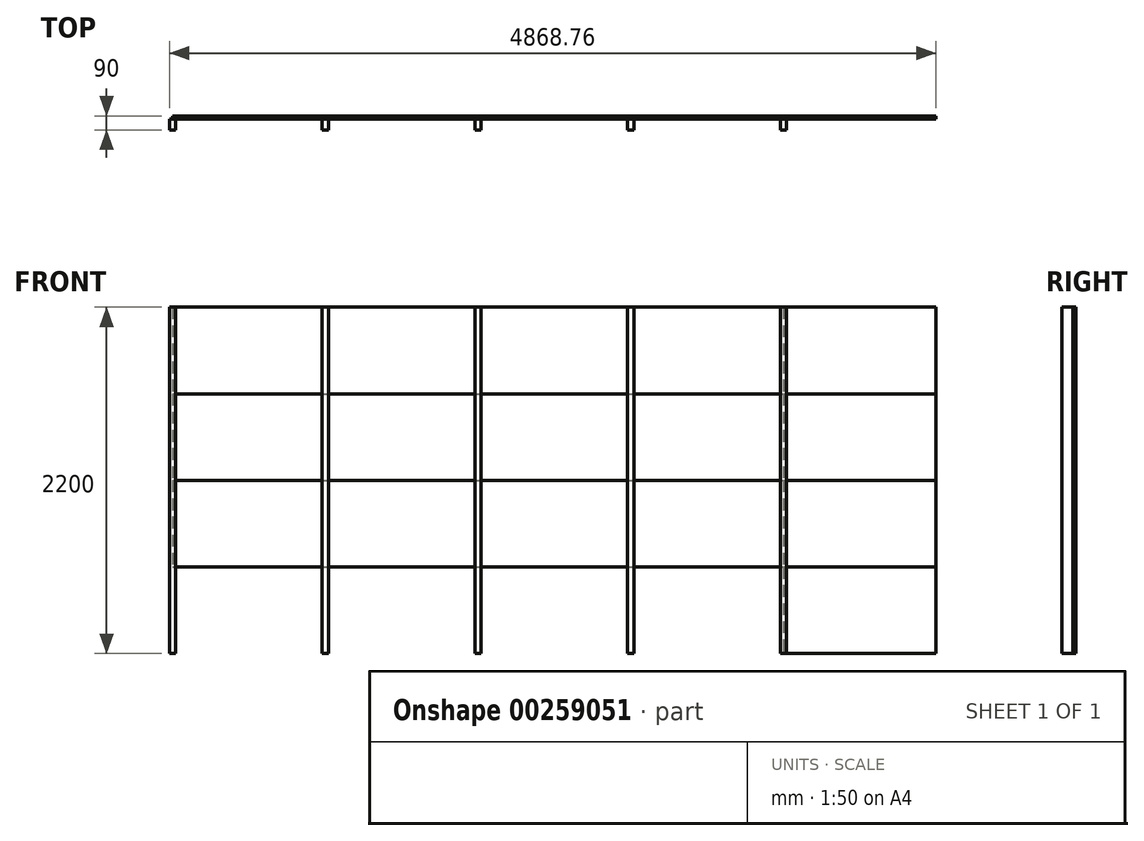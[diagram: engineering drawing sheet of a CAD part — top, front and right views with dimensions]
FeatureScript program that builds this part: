
annotation { "Feature Type Name" : "Feature", "Feature Type Description" : "" }
export const myFeature = defineFeature(function(context is Context, id is Id, definition is map)
    precondition{}
    {
        {
            var Q0;
            Q0=qCreatedBy(makeId("Top.planeOp"),FACE);
            var sketch = newSketch(context, id + "F0", { "sketchPlane" : qUnion([Q0])});
            skLineSegment(sketch, "E0.bottom", {"start": v(0, 0) * mm, "end": v(40, 0) * mm});
            skLineSegment(sketch, "E0.top", {"start": v(0, 70) * mm, "end": v(40, 70) * mm});
            skLineSegment(sketch, "E0.left", {"start": v(0, 0) * mm, "end": v(0, 70) * mm});
            skLineSegment(sketch, "E0.right", {"start": v(40, 0) * mm, "end": v(40, 70) * mm});
            skLineSegment(sketch, "E1.bottom", {"start": v(0, 70) * mm, "end": v(3920, 70) * mm});
            skLineSegment(sketch, "E1.top", {"start": v(20, 90) * mm, "end": v(3900, 90) * mm});
            skLineSegment(sketch, "E2.bottom", {"start": v(20, 70) * mm, "end": v(990, 70) * mm});
            skLineSegment(sketch, "E2.top", {"start": v(20, 90) * mm, "end": v(990, 90) * mm});
            skLineSegment(sketch, "E2.left", {"start": v(20, 70) * mm, "end": v(20, 90) * mm});
            skLineSegment(sketch, "E2.right", {"start": v(990, 70) * mm, "end": v(990, 90) * mm});
            skLineSegment(sketch, "E3.bottom", {"start": v(990, 70) * mm, "end": v(1960, 70) * mm});
            skLineSegment(sketch, "E3.top", {"start": v(990, 90) * mm, "end": v(1960, 90) * mm});
            skLineSegment(sketch, "E3.right", {"start": v(1960, 70) * mm, "end": v(1960, 90) * mm});
            skLineSegment(sketch, "E4.bottom", {"start": v(1960, 70) * mm, "end": v(2930, 70) * mm});
            skLineSegment(sketch, "E4.top", {"start": v(1960, 90) * mm, "end": v(2930, 90) * mm});
            skLineSegment(sketch, "E4.right", {"start": v(2930, 70) * mm, "end": v(2930, 90) * mm});
            skLineSegment(sketch, "E5.bottom", {"start": v(2930, 70) * mm, "end": v(3900, 70) * mm});
            skLineSegment(sketch, "E5.top", {"start": v(2930, 90) * mm, "end": v(3900, 90) * mm});
            skLineSegment(sketch, "E5.right", {"start": v(3900, 70) * mm, "end": v(3900, 90) * mm});
            skLineSegment(sketch, "E6.bottom", {"start": v(3880, 70) * mm, "end": v(3920, 70) * mm});
            skLineSegment(sketch, "E6.top", {"start": v(3880, 0) * mm, "end": v(3920, 0) * mm});
            skLineSegment(sketch, "E6.left", {"start": v(3880, 70) * mm, "end": v(3880, 0) * mm});
            skLineSegment(sketch, "E6.right", {"start": v(3920, 70) * mm, "end": v(3920, 0) * mm});
            skLineSegment(sketch, "E7.bottom", {"start": v(970, 70) * mm, "end": v(1010, 70) * mm});
            skLineSegment(sketch, "E7.top", {"start": v(970, 0) * mm, "end": v(1010, 0) * mm});
            skLineSegment(sketch, "E7.left", {"start": v(970, 70) * mm, "end": v(970, 0) * mm});
            skLineSegment(sketch, "E7.right", {"start": v(1010, 70) * mm, "end": v(1010, 0) * mm});
            skLineSegment(sketch, "E8.bottom", {"start": v(1940, 70) * mm, "end": v(1980, 70) * mm});
            skLineSegment(sketch, "E8.top", {"start": v(1940, 0) * mm, "end": v(1980, 0) * mm});
            skLineSegment(sketch, "E8.left", {"start": v(1940, 70) * mm, "end": v(1940, 0) * mm});
            skLineSegment(sketch, "E8.right", {"start": v(1980, 70) * mm, "end": v(1980, 0) * mm});
            skLineSegment(sketch, "E9.bottom", {"start": v(2910, 70) * mm, "end": v(2950, 70) * mm});
            skLineSegment(sketch, "E9.top", {"start": v(2910, 0) * mm, "end": v(2950, 0) * mm});
            skLineSegment(sketch, "E9.left", {"start": v(2910, 70) * mm, "end": v(2910, 0) * mm});
            skLineSegment(sketch, "E9.right", {"start": v(2950, 70) * mm, "end": v(2950, 0) * mm});
            skLineSegment(sketch, "E10.right", {"start": v(3898.76, 70.38) * mm, "end": v(3898.76, 90.38) * mm});
            skLineSegment(sketch, "E11.bottom", {"start": v(3898.76, 70.38) * mm, "end": v(4868.76, 70.38) * mm});
            skLineSegment(sketch, "E11.right", {"start": v(4868.76, 70.38) * mm, "end": v(4868.76, 90) * mm});
            skLineSegment(sketch, "E12.top", {"start": v(4848.76, 0.38) * mm, "end": v(4888.76, 0.38) * mm});
            skLineSegment(sketch, "E12.left", {"start": v(4848.76, 70.38) * mm, "end": v(4848.76, 0.38) * mm});
            skLineSegment(sketch, "E12.right", {"start": v(4888.76, 70.38) * mm, "end": v(4888.76, 0.38) * mm});
            skLineSegment(sketch, "E13.bottom", {"start": v(3900, 70) * mm, "end": v(4868.76, 70) * mm});
            skLineSegment(sketch, "E13.top", {"start": v(3900, 90) * mm, "end": v(4868.76, 90) * mm});
            skLineSegment(sketch, "E13.right", {"start": v(4868.76, 70) * mm, "end": v(4868.76, 90) * mm});
            skLineSegment(sketch, "E14.top", {"start": v(4848.76, 70.38) * mm, "end": v(4888.76, 70.38) * mm});
            skLineSegment(sketch, "E14.left", {"start": v(4848.76, 0.38) * mm, "end": v(4848.76, 70.38) * mm});
            skLineSegment(sketch, "E14.right", {"start": v(4888.76, 0.38) * mm, "end": v(4888.76, 70.38) * mm});
            skSolve(sketch);
        }
        {
            var Q0;
            Q0=makeQuery(id+"F0.imprint","IMPRINT",FACE,{"disambiguationData":[TD([[makeQuery(id+"F0.imprint","IMPRINT",EDGE,{"derivedFrom":sQuery(id+"F0.wireOp",EDGE,"E0.bottom")}),1.0]])]});
            var Q1;
            Q1=makeQuery(id+"F0.imprint","IMPRINT",FACE,{"disambiguationData":[TD([[makeQuery(id+"F0.imprint","IMPRINT",EDGE,{"derivedFrom":sQuery(id+"F0.wireOp",EDGE,"E7.top")}),1.0]])]});
            var Q2;
            Q2=makeQuery(id+"F0.imprint","IMPRINT",FACE,{"disambiguationData":[TD([[makeQuery(id+"F0.imprint","IMPRINT",EDGE,{"derivedFrom":sQuery(id+"F0.wireOp",EDGE,"E8.top")}),1.0]])]});
            var Q3;
            Q3=makeQuery(id+"F0.imprint","IMPRINT",FACE,{"disambiguationData":[TD([[makeQuery(id+"F0.imprint","IMPRINT",EDGE,{"derivedFrom":sQuery(id+"F0.wireOp",EDGE,"E9.top")}),1.0]])]});
            var Q4;
            Q4=makeQuery(id+"F0.imprint","IMPRINT",FACE,{"disambiguationData":[TD([[makeQuery(id+"F0.imprint","IMPRINT",EDGE,{"derivedFrom":sQuery(id+"F0.wireOp",EDGE,"E6.top")}),1.0]])]});
            var Q5;
            {var subQ4=sQuery(id+"F0.wireOp",EDGE,"E12.top");Q5=makeQuery(id+"F0.imprint","IMPRINT",FACE,{"disambiguationData":[TD([[makeQuery(id+"F0.imprint","IMPRINT",EDGE,{"derivedFrom":subQ4}),1.0]])]});}
            extrude(context, id + "F1", {"entities" : qUnion([Q0, Q1, Q2, Q3, Q4, Q5]), "depth" : 2200 * mm});
        }
        {
            var Q0;
            Q0=makeQuery(id+"F0.imprint","IMPRINT",FACE,{"disambiguationData":[TD([[makeQuery(id+"F0.imprint","IMPRINT",EDGE,{"derivedFrom":sQuery(id+"F0.wireOp",EDGE,"E2.top")}),-1.0]])]});
            var Q1;
            {var subQ2=sQuery(id+"F0.wireOp",EDGE,"E3.bottom");Q1=makeQuery(id+"F0.imprint","IMPRINT",FACE,{"disambiguationData":[TD([[makeQuery(id+"F0.imprint","IMPRINT",EDGE,{"derivedFrom":subQ2}),1.0]])]});}
            var Q2;
            {var subQ2=sQuery(id+"F0.wireOp",EDGE,"E4.bottom");Q2=makeQuery(id+"F0.imprint","IMPRINT",FACE,{"disambiguationData":[TD([[makeQuery(id+"F0.imprint","IMPRINT",EDGE,{"derivedFrom":subQ2}),1.0]])]});}
            var Q3;
            {var subQ2=sQuery(id+"F0.wireOp",EDGE,"E5.bottom");Q3=makeQuery(id+"F0.imprint","IMPRINT",FACE,{"disambiguationData":[TD([[makeQuery(id+"F0.imprint","IMPRINT",EDGE,{"derivedFrom":subQ2}),1.0]])]});}
            var Q4;
            {var subQ1=sQuery(id+"F0.wireOp",EDGE,"E13.top");Q4=makeQuery(id+"F0.imprint","IMPRINT",FACE,{"disambiguationData":[TD([[makeQuery(id+"F0.imprint","IMPRINT",EDGE,{"derivedFrom":subQ1}),-1.0]])]});}
            extrude(context, id + "F2", {"entities" : qUnion([Q0, Q1, Q2, Q3, Q4]), "depth" : 550 * mm});
        }
        {
            var Q0;
            Q0=makeQuery(id+"F2.opExtrude","CAP_FACE",FACE,{"disambiguationData":[OSD([sQuery(id+"F0.wireOp",EDGE,"E2.bottom"),sQuery(id+"F0.wireOp",EDGE,"E2.top"),sQuery(id+"F0.wireOp",EDGE,"E2.left"),sQuery(id+"F0.wireOp",EDGE,"E3.bottom"),sQuery(id+"F0.wireOp",EDGE,"E3.top"),sQuery(id+"F0.wireOp",EDGE,"E4.bottom"),sQuery(id+"F0.wireOp",EDGE,"E4.top"),sQuery(id+"F0.wireOp",EDGE,"E5.bottom"),sQuery(id+"F0.wireOp",EDGE,"E5.top"),sQuery(id+"F0.wireOp",EDGE,"E5.right"),sQuery(id+"F0.wireOp",EDGE,"E6.bottom"),sQuery(id+"F0.wireOp",EDGE,"E7.bottom"),sQuery(id+"F0.wireOp",EDGE,"E8.bottom"),sQuery(id+"F0.wireOp",EDGE,"E9.bottom")])],"isStart":false});
            var sketch = newSketch(context, id + "F3", { "sketchPlane" : qUnion([Q0])});
            skLineSegment(sketch, "E15.0", {"start": v(20, 70) * mm, "end": v(3900, 70) * mm});
            skLineSegment(sketch, "E16.bottom", {"start": v(20, 70) * mm, "end": v(3898.76, 70) * mm});
            skLineSegment(sketch, "E16.top", {"start": v(20, 90) * mm, "end": v(3898.76, 90) * mm});
            skLineSegment(sketch, "E16.left", {"start": v(20, 70) * mm, "end": v(20, 90) * mm});
            skLineSegment(sketch, "E16.right", {"start": v(3898.76, 70) * mm, "end": v(3898.76, 90) * mm});
            skSolve(sketch);
        }
        {
            var Q0;
            Q0 = qSketchRegion(id + "F3", true);
            var Q1;
            Q1=makeQuery(id+"F2.opExtrude","CAP_FACE",FACE,{"disambiguationData":[OSD([sQuery(id+"F0.wireOp",EDGE,"E11.bottom"),sQuery(id+"F0.wireOp",EDGE,"E13.top"),sQuery(id+"F0.wireOp",EDGE,"E5.right"),sQuery(id+"F0.wireOp",EDGE,"E13.right"),sQuery(id+"F0.wireOp",EDGE,"E14.top")])],"isStart":false});
            extrude(context, id + "F4", {"entities" : qUnion([Q0, Q1]), "depth" : 550 * mm});
        }
        {
            var Q0;
            Q0=makeQuery(id+"F4.opExtrude","CAP_FACE",FACE,{"disambiguationData":[OSD([sQuery(id+"F3.wireOp",EDGE,"E16.bottom"),sQuery(id+"F3.wireOp",EDGE,"E16.top"),sQuery(id+"F3.wireOp",EDGE,"E16.left"),sQuery(id+"F3.wireOp",EDGE,"E16.right")])],"isStart":false});
            var sketch = newSketch(context, id + "F5", { "sketchPlane" : qUnion([Q0])});
            skLineSegment(sketch, "E17.0.0", {"start": v(20, 90) * mm, "end": v(20, 70) * mm});
            skLineSegment(sketch, "E17.0.1", {"start": v(20, 70) * mm, "end": v(3898.76, 70) * mm});
            skLineSegment(sketch, "E17.0.2", {"start": v(3898.76, 70) * mm, "end": v(3898.76, 90) * mm});
            skLineSegment(sketch, "E17.0.3", {"start": v(3898.76, 90) * mm, "end": v(20, 90) * mm});
            skSolve(sketch);
        }
        {
            var Q0;
            Q0=makeQuery(id+"F5.imprint","IMPRINT",FACE,{"disambiguationData":[TD([[makeQuery(id+"F5.imprint","IMPRINT",EDGE,{"derivedFrom":sQuery(id+"F5.wireOp",EDGE,"E17.0.0")}),-1.0]])]});
            var Q1;
            Q1=makeQuery(id+"F4.opExtrude","CAP_FACE",FACE,{"disambiguationData":[OSD([sQuery(id+"F0.wireOp",EDGE,"E11.bottom"),sQuery(id+"F0.wireOp",EDGE,"E13.top"),sQuery(id+"F0.wireOp",EDGE,"E5.right"),sQuery(id+"F0.wireOp",EDGE,"E13.right"),sQuery(id+"F0.wireOp",EDGE,"E14.top")])],"isStart":false});
            extrude(context, id + "F6", {"entities" : qUnion([Q0, Q1]), "depth" : 550 * mm});
        }
        {
            var Q0;
            Q0=makeQuery(id+"F6.opExtrude","CAP_FACE",FACE,{"disambiguationData":[OSD([sQuery(id+"F5.wireOp",EDGE,"E17.0.0"),sQuery(id+"F5.wireOp",EDGE,"E17.0.1"),sQuery(id+"F5.wireOp",EDGE,"E17.0.2"),sQuery(id+"F5.wireOp",EDGE,"E17.0.3")])],"isStart":false});
            var sketch = newSketch(context, id + "F7", { "sketchPlane" : qUnion([Q0])});
            skLineSegment(sketch, "E18.0", {"start": v(20, 90) * mm, "end": v(3898.76, 90) * mm});
            skSolve(sketch);
        }
        {
            var Q0;
            Q0 = qSketchRegion(id + "F7", true);
            var Q1;
            Q1=makeQuery(id+"F7.imprint","IMPRINT",FACE,{"disambiguationData":[TD([[makeQuery(id+"F7.imprint","IMPRINT",EDGE,{"derivedFrom":sQuery(id+"F7.wireOp",EDGE,"E18.0")}),-1.0]])]});
            var Q2;
            Q2=makeQuery(id+"F6.opExtrude","CAP_FACE",FACE,{"disambiguationData":[OSD([sQuery(id+"F0.wireOp",EDGE,"E11.bottom"),sQuery(id+"F0.wireOp",EDGE,"E13.top"),sQuery(id+"F0.wireOp",EDGE,"E5.right"),sQuery(id+"F0.wireOp",EDGE,"E13.right"),sQuery(id+"F0.wireOp",EDGE,"E14.top")])],"isStart":false});
            extrude(context, id + "F8", {"entities" : qUnion([Q0, Q1, Q2]), "depth" : 550 * mm});
        }
    });
